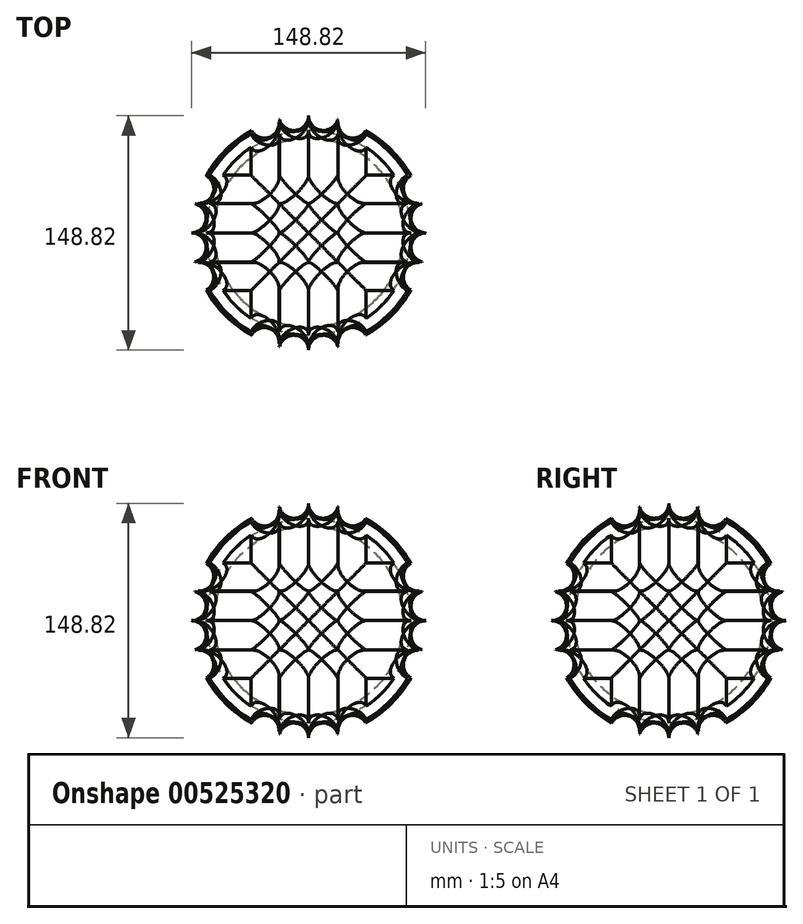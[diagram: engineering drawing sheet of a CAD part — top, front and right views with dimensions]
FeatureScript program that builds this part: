
annotation { "Feature Type Name" : "Feature", "Feature Type Description" : "" }
export const myFeature = defineFeature(function(context is Context, id is Id, definition is map)
    precondition{}
    {
        {
            var Q0;
            Q0=qCreatedBy(makeId("Top.planeOp"),FACE);
            var sketch = newSketch(context, id + "F0", { "sketchPlane" : qUnion([Q0])});
            skCircle(sketch, "E0", {"center": v(0, 0) * mm, "radius": 75 * mm});
            skLineSegment(sketch, "E1", {"start": v(-75, 0) * mm, "end": v(75, 0) * mm});
            skLineSegment(sketch, "E2", {"start": v(75, 0) * mm, "end": v(0, 0) * mm, "construction": true});
            skLineSegment(sketch, "E3", {"start": v(0, 0) * mm, "end": v(0, 75) * mm, "construction": true});
            skLineSegment(sketch, "E4.bottom", {"start": v(75, 75) * mm, "end": v(-75, 75) * mm, "construction": true});
            skLineSegment(sketch, "E4.top", {"start": v(75, -75) * mm, "end": v(-75, -75) * mm, "construction": true});
            skLineSegment(sketch, "E4.left", {"start": v(75, 75) * mm, "end": v(75, -75) * mm, "construction": true});
            skLineSegment(sketch, "E4.right", {"start": v(-75, 75) * mm, "end": v(-75, -75) * mm, "construction": true});
            skLineSegment(sketch, "E5", {"start": v(0, 75) * mm, "end": v(75, 75) * mm, "construction": true});
            skLineSegment(sketch, "E6", {"start": v(37.5, 75) * mm, "end": v(0, 75) * mm, "construction": true});
            skLineSegment(sketch, "E7", {"start": v(0, 75) * mm, "end": v(-75, 75) * mm, "construction": true});
            skLineSegment(sketch, "E8", {"start": v(0, 75) * mm, "end": v(-37.5, 75) * mm, "construction": true});
            skCircle(sketch, "E9", {"center": v(-9.38, 75) * mm, "radius": 9.38 * mm, "construction": true});
            skPoint(sketch, "E9.second.point", {"position": v(-18.75, 75) * mm});
            skPoint(sketch, "E9.third.point", {"position": v(-8.67, 65.65) * mm});
            skCircle(sketch, "E10", {"center": v(-28.12, 75) * mm, "radius": 9.38 * mm, "construction": true});
            skPoint(sketch, "E10.third.point", {"position": v(-24.28, 83.55) * mm});
            skCircle(sketch, "E11", {"center": v(9.38, 75) * mm, "radius": 9.38 * mm, "construction": true});
            skPoint(sketch, "E11.second.point", {"position": v(18.75, 75) * mm});
            skPoint(sketch, "E11.third.point", {"position": v(10.65, 84.29) * mm});
            skCircle(sketch, "E12", {"center": v(28.12, 75) * mm, "radius": 9.38 * mm, "construction": true});
            skPoint(sketch, "E12.third.point", {"position": v(29, 84.33) * mm});
            skLineSegment(sketch, "E13", {"start": v(37.5, 75) * mm, "end": v(37.5, 0) * mm, "construction": true});
            skLineSegment(sketch, "E14", {"start": v(18.75, 75) * mm, "end": v(18.75, 0) * mm, "construction": true});
            skLineSegment(sketch, "E15", {"start": v(-18.75, 75) * mm, "end": v(-18.75, 0) * mm, "construction": true});
            skLineSegment(sketch, "E16", {"start": v(-37.5, 75) * mm, "end": v(-37.5, 0) * mm, "construction": true});
            skCircle(sketch, "E17", {"center": v(-28.12, 69.53) * mm, "radius": 9.38 * mm});
            skCircle(sketch, "E18", {"center": v(-9.38, 74.41) * mm, "radius": 9.38 * mm});
            skCircle(sketch, "E19", {"center": v(9.38, 74.41) * mm, "radius": 9.38 * mm});
            skCircle(sketch, "E20", {"center": v(28.12, 69.53) * mm, "radius": 9.37 * mm});
            skLineSegment(sketch, "E21", {"start": v(18.75, 69.53) * mm, "end": v(18.75, 75) * mm});
            skLineSegment(sketch, "E22", {"start": v(-18.75, 69.53) * mm, "end": v(-18.75, 75) * mm});
            skSolve(sketch);
        }
        {
            var Q0;
            {var subQ0=sQuery(id+"F0.wireOp",EDGE,"E1");Q0=makeQuery(id+"F0.imprint","IMPRINT",FACE,{"disambiguationData":[TD([[makeQuery(id+"F0.imprint","IMPRINT",EDGE,{"derivedFrom":subQ0}),1.0]])]});}
            var Q1;
            Q1=sQuery(id+"F0.wireOp",EDGE,"E2");
            revolve(context, id + "F1", {"surfaceOperationType" : NewSurfaceOperationType.NEW, "entities" : qUnion([Q0]), "axis" : qUnion([Q1]), "revolveType" : RevolveType.FULL});
        }
        {
            var Q0;
            Q0=makeQuery(id+"F1.opRevolve","SWEPT_BODY",BODY,{"disambiguationData":[OSD([sQuery(id+"F0.wireOp",EDGE,"E0"),sQuery(id+"F0.wireOp",EDGE,"E1"),sQuery(id+"F0.wireOp",EDGE,"E17"),sQuery(id+"F0.wireOp",EDGE,"E18"),sQuery(id+"F0.wireOp",EDGE,"E19"),sQuery(id+"F0.wireOp",EDGE,"E20"),sQuery(id+"F0.wireOp",EDGE,"E21"),sQuery(id+"F0.wireOp",EDGE,"E22")])]});
            var Q1;
            Q1=sQuery(id+"F0.wireOp",EDGE,"E3");
            transform(context, id + "F2", {"entities" : qUnion([Q0]), "transformType" : TransformType.ROTATION, "transformAxis" : qUnion([Q1]), "angle" : 90 * degree, "makeCopy" : true});
        }
        {
            var Q0;
            Q0=makeQuery(id+"F2.opPattern","COPY",BODY,{"derivedFrom":makeQuery(id+"F1.opRevolve","SWEPT_BODY",BODY,{"disambiguationData":[OSD([sQuery(id+"F0.wireOp",EDGE,"E0"),sQuery(id+"F0.wireOp",EDGE,"E1"),sQuery(id+"F0.wireOp",EDGE,"E17"),sQuery(id+"F0.wireOp",EDGE,"E18"),sQuery(id+"F0.wireOp",EDGE,"E19"),sQuery(id+"F0.wireOp",EDGE,"E20"),sQuery(id+"F0.wireOp",EDGE,"E21"),sQuery(id+"F0.wireOp",EDGE,"E22")])]}),"instanceName":"1"});
            var Q1;
            Q1=sQuery(id+"F0.wireOp",EDGE,"E1");
            transform(context, id + "F3", {"entities" : qUnion([Q0]), "transformType" : TransformType.ROTATION, "transformAxis" : qUnion([Q1]), "angle" : 90 * degree, "makeCopy" : true});
        }
        {
            var Q0;
            Q0=makeQuery(id+"F1.opRevolve","SWEPT_BODY",BODY,{"disambiguationData":[OSD([sQuery(id+"F0.wireOp",EDGE,"E0"),sQuery(id+"F0.wireOp",EDGE,"E1"),sQuery(id+"F0.wireOp",EDGE,"E17"),sQuery(id+"F0.wireOp",EDGE,"E18"),sQuery(id+"F0.wireOp",EDGE,"E19"),sQuery(id+"F0.wireOp",EDGE,"E20"),sQuery(id+"F0.wireOp",EDGE,"E21"),sQuery(id+"F0.wireOp",EDGE,"E22")])]});
            var Q1;
            Q1=makeQuery(id+"F2.opPattern","COPY",BODY,{"derivedFrom":makeQuery(id+"F1.opRevolve","SWEPT_BODY",BODY,{"disambiguationData":[OSD([sQuery(id+"F0.wireOp",EDGE,"E0"),sQuery(id+"F0.wireOp",EDGE,"E1"),sQuery(id+"F0.wireOp",EDGE,"E17"),sQuery(id+"F0.wireOp",EDGE,"E18"),sQuery(id+"F0.wireOp",EDGE,"E19"),sQuery(id+"F0.wireOp",EDGE,"E20"),sQuery(id+"F0.wireOp",EDGE,"E21"),sQuery(id+"F0.wireOp",EDGE,"E22")])]}),"instanceName":"1"});
            var Q2;
            Q2=makeQuery(id+"F3.opPattern","COPY",BODY,{"derivedFrom":makeQuery(id+"F2.opPattern","COPY",BODY,{"derivedFrom":makeQuery(id+"F1.opRevolve","SWEPT_BODY",BODY,{"disambiguationData":[OSD([sQuery(id+"F0.wireOp",EDGE,"E0"),sQuery(id+"F0.wireOp",EDGE,"E1"),sQuery(id+"F0.wireOp",EDGE,"E17"),sQuery(id+"F0.wireOp",EDGE,"E18"),sQuery(id+"F0.wireOp",EDGE,"E19"),sQuery(id+"F0.wireOp",EDGE,"E20"),sQuery(id+"F0.wireOp",EDGE,"E21"),sQuery(id+"F0.wireOp",EDGE,"E22")])]}),"instanceName":"1"}),"instanceName":"1"});
            booleanBodies(context, id + "F4", {"operationType" : BooleanOperationType.INTERSECTION, "tools" : qUnion([Q0, Q1, Q2])});
        }
    });
